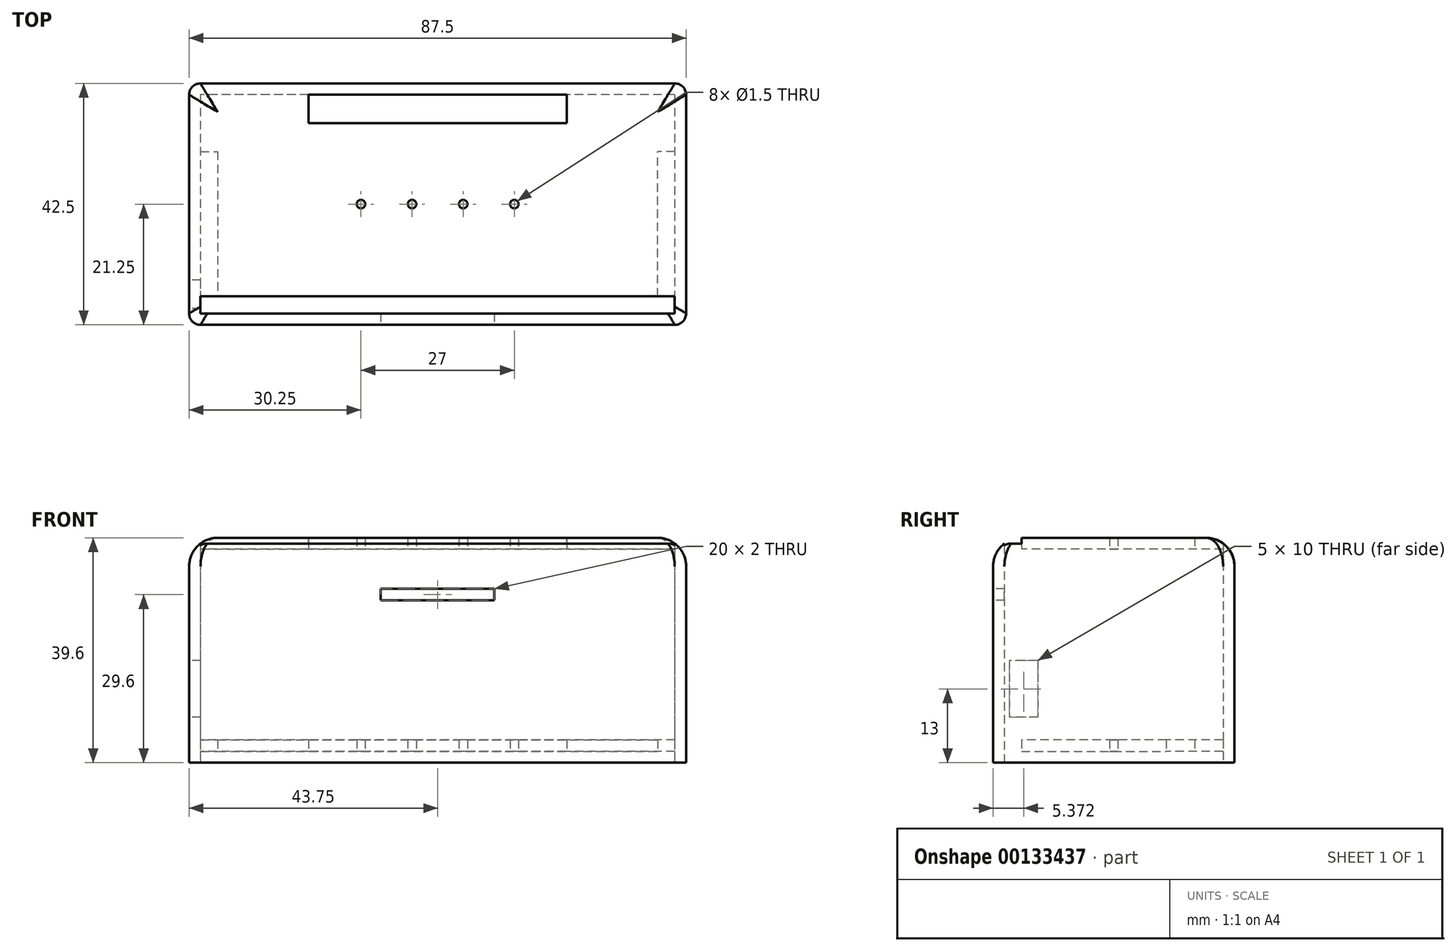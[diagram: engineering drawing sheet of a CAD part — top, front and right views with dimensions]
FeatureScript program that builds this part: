
annotation { "Feature Type Name" : "Feature", "Feature Type Description" : "" }
export const myFeature = defineFeature(function(context is Context, id is Id, definition is map)
    precondition{}
    {
        {
            var Q0;
            Q0=qCreatedBy(makeId("Top.planeOp"),FACE);
            var sketch = newSketch(context, id + "F0", { "sketchPlane" : qUnion([Q0])});
            skLineSegment(sketch, "E0.bottom", {"start": v(43.75, 21.25) * mm, "end": v(-43.75, 21.25) * mm});
            skLineSegment(sketch, "E0.top", {"start": v(43.75, -21.25) * mm, "end": v(-43.75, -21.25) * mm});
            skLineSegment(sketch, "E0.left", {"start": v(43.75, 21.25) * mm, "end": v(43.75, -21.25) * mm});
            skLineSegment(sketch, "E0.right", {"start": v(-43.75, 21.25) * mm, "end": v(-43.75, -21.25) * mm});
            skPoint(sketch, "E0.middle", {"position": v(0, 0) * mm});
            skLineSegment(sketch, "E1.0", {"start": v(-41.75, 19.25) * mm, "end": v(-41.75, -19.25) * mm});
            skLineSegment(sketch, "E1.1", {"start": v(41.75, 19.25) * mm, "end": v(-41.75, 19.25) * mm});
            skLineSegment(sketch, "E1.2", {"start": v(41.75, 19.25) * mm, "end": v(41.75, -19.25) * mm});
            skLineSegment(sketch, "E1.3", {"start": v(41.75, -19.25) * mm, "end": v(-41.75, -19.25) * mm});
            skLineSegment(sketch, "E2", {"start": v(0, 0) * mm, "end": v(4.5, 0) * mm});
            skLineSegment(sketch, "E3", {"start": v(4.5, 0) * mm, "end": v(13.5, 0) * mm});
            skCircle(sketch, "E4", {"center": v(4.5, 0) * mm, "radius": 0.75 * mm});
            skCircle(sketch, "E5", {"center": v(13.5, 0) * mm, "radius": 0.75 * mm});
            skCircle(sketch, "E6.MirrorC", {"center": v(-4.5, 0) * mm, "radius": 0.75 * mm});
            skCircle(sketch, "E7.MirrorC", {"center": v(-13.5, 0) * mm, "radius": 0.75 * mm});
            skLineSegment(sketch, "E8.bottom", {"start": v(-41.75, -19.25) * mm, "end": v(41.75, -19.25) * mm});
            skLineSegment(sketch, "E8.top", {"start": v(-41.75, -16.25) * mm, "end": v(41.75, -16.25) * mm});
            skLineSegment(sketch, "E8.left", {"start": v(-41.75, -19.25) * mm, "end": v(-41.75, -16.25) * mm});
            skLineSegment(sketch, "E8.right", {"start": v(41.75, -19.25) * mm, "end": v(41.75, -16.25) * mm});
            skLineSegment(sketch, "E9", {"start": v(-41.75, -16.25) * mm, "end": v(-38.75, -16.25) * mm});
            skLineSegment(sketch, "E10", {"start": v(-38.75, -16.25) * mm, "end": v(-38.75, 0) * mm});
            skLineSegment(sketch, "E11", {"start": v(41.75, -16.25) * mm, "end": v(38.75, -16.25) * mm});
            skLineSegment(sketch, "E12", {"start": v(38.75, -16.25) * mm, "end": v(38.75, -16.25) * mm});
            skLineSegment(sketch, "E13", {"start": v(38.75, -16.25) * mm, "end": v(38.75, 0) * mm});
            skLineSegment(sketch, "E14", {"start": v(-41.75, -16.25) * mm, "end": v(-41.75, 0) * mm});
            skLineSegment(sketch, "E15", {"start": v(-41.75, 19.25) * mm, "end": v(-22.75, 19.25) * mm});
            skLineSegment(sketch, "E16", {"start": v(-22.75, 19.25) * mm, "end": v(-22.75, 14.25) * mm});
            skLineSegment(sketch, "E17", {"start": v(41.75, 19.25) * mm, "end": v(22.75, 19.25) * mm});
            skLineSegment(sketch, "E18", {"start": v(22.75, 19.25) * mm, "end": v(22.75, 14.25) * mm});
            skLineSegment(sketch, "E19", {"start": v(22.75, 14.25) * mm, "end": v(-22.75, 14.25) * mm});
            skLineSegment(sketch, "E20", {"start": v(-41.75, 19.25) * mm, "end": v(-41.75, 9.25) * mm});
            skLineSegment(sketch, "E21", {"start": v(-41.75, 9.25) * mm, "end": v(-38.75, 9.25) * mm});
            skLineSegment(sketch, "E22", {"start": v(-38.75, 9.25) * mm, "end": v(-38.75, 0) * mm});
            skLineSegment(sketch, "E23", {"start": v(41.75, 19.25) * mm, "end": v(41.75, 9.25) * mm});
            skLineSegment(sketch, "E24", {"start": v(41.75, 9.25) * mm, "end": v(38.75, 9.25) * mm});
            skLineSegment(sketch, "E25", {"start": v(38.75, 9.25) * mm, "end": v(38.75, 0) * mm});
            skLineSegment(sketch, "E26", {"start": v(-41.75, 0) * mm, "end": v(-41.75, -19.25) * mm});
            skSolve(sketch);
        }
        {
            var Q0;
            Q0=makeQuery(id+"F0.imprint","IMPRINT",FACE,{"disambiguationData":[TD([[makeQuery(id+"F0.imprint","IMPRINT",EDGE,{"derivedFrom":sQuery(id+"F0.wireOp",EDGE,"E0.bottom")}),1.0]])]});
            extrude(context, id + "F1", {"entities" : qUnion([Q0]), "depth" : 39.6 * mm});
        }
        {
            var Q0;
            Q0=makeQuery(id+"F0.imprint","IMPRINT",FACE,{"disambiguationData":[TD([[makeQuery(id+"F0.imprint","IMPRINT",EDGE,{"derivedFrom":sQuery(id+"F0.wireOp",EDGE,"E1.0")}),1.0]])]});
            var Q1;
            Q1=makeQuery(id+"F0.imprint","IMPRINT",FACE,{"disambiguationData":[TD([[makeQuery(id+"F0.imprint","IMPRINT",EDGE,{"derivedFrom":sQuery(id+"F0.wireOp",EDGE,"E5")}),-1.0]])]});
            var Q2;
            Q2=makeQuery(id+"F0.imprint","IMPRINT",FACE,{"disambiguationData":[TD([[makeQuery(id+"F0.imprint","IMPRINT",EDGE,{"derivedFrom":sQuery(id+"F0.wireOp",EDGE,"E1.2")}),-1.0]])]});
            var Q3;
            Q3=makeQuery(id+"F0.imprint","IMPRINT",FACE,{"disambiguationData":[TD([[makeQuery(id+"F0.imprint","IMPRINT",EDGE,{"derivedFrom":sQuery(id+"F0.wireOp",EDGE,"E1.1")}),1.0]])]});
            var Q4;
            Q4=makeQuery(id+"F0.imprint","IMPRINT",FACE,{"disambiguationData":[TD([[makeQuery(id+"F0.imprint","IMPRINT",EDGE,{"derivedFrom":sQuery(id+"F0.wireOp",EDGE,"E8.bottom")}),1.0]])]});
            extrude(context, id + "F2", {"entities" : qUnion([Q0, Q1, Q2, Q3, Q4]), "operationType" : NewBodyOperationType.ADD, "depth" : 39.6 * mm, "hasSecondDirection" : true, "secondDirectionOppositeDirection" : false, "secondDirectionDepth" : 37.6 * mm});
        }
        {
            var Q0;
            Q0 = qSketchRegion(id + "F0", true);
            var Q1;
            Q1=makeQuery(id+"F0.imprint","IMPRINT",FACE,{"disambiguationData":[TD([[makeQuery(id+"F0.imprint","IMPRINT",EDGE,{"derivedFrom":sQuery(id+"F0.wireOp",EDGE,"E9")}),1.0]])]});
            var Q2;
            Q2=makeQuery(id+"F0.imprint","IMPRINT",FACE,{"disambiguationData":[TD([[makeQuery(id+"F0.imprint","IMPRINT",EDGE,{"derivedFrom":sQuery(id+"F0.wireOp",EDGE,"E8.bottom")}),1.0]])]});
            var Q3;
            {var subQ0=sQuery(id+"F0.wireOp",EDGE,"E11");Q3=makeQuery(id+"F0.imprint","IMPRINT",FACE,{"disambiguationData":[TD([[makeQuery(id+"F0.imprint","IMPRINT",EDGE,{"derivedFrom":subQ0}),-1.0]])]});}
            var Q4;
            Q4=makeQuery(id+"F0.imprint","IMPRINT",FACE,{"disambiguationData":[TD([[makeQuery(id+"F0.imprint","IMPRINT",EDGE,{"derivedFrom":sQuery(id+"F0.wireOp",EDGE,"E1.1")}),1.0]])]});
            extrude(context, id + "F3", {"entities" : qUnion([Q0, Q1, Q2, Q3, Q4]), "operationType" : NewBodyOperationType.ADD, "depth" : 4 * mm, "hasSecondDirection" : true, "secondDirectionOppositeDirection" : false, "secondDirectionDepth" : 2 * mm});
        }
        {
            var Q0;
            Q0=makeQuery(id+"F1.opExtrude","SWEPT_EDGE",EDGE,{"disambiguationData":[OSD([sQuery(id+"F0.wireOp",EDGE,"E0.bottom"),sQuery(id+"F0.wireOp",EDGE,"E0.left")])]});
            var Q1;
            Q1=makeQuery(id+"F1.opExtrude","SWEPT_EDGE",EDGE,{"disambiguationData":[OSD([sQuery(id+"F0.wireOp",EDGE,"E0.bottom"),sQuery(id+"F0.wireOp",EDGE,"E0.right")])]});
            var Q2;
            Q2=makeQuery(id+"F1.opExtrude","SWEPT_EDGE",EDGE,{"disambiguationData":[OSD([sQuery(id+"F0.wireOp",EDGE,"E0.top"),sQuery(id+"F0.wireOp",EDGE,"E0.left")])]});
            var Q3;
            Q3=makeQuery(id+"F1.opExtrude","SWEPT_EDGE",EDGE,{"disambiguationData":[OSD([sQuery(id+"F0.wireOp",EDGE,"E0.top"),sQuery(id+"F0.wireOp",EDGE,"E0.right")])]});
            fillet(context, id + "F4", {"entities" : qUnion([Q0, Q1, Q2, Q3]), "radius" : 2 * mm, "tangentPropagation" : true, "allowEdgeOverflow" : false});
        }
        {
            var Q0;
            Q0=makeQuery(id+"F1.opExtrude","CAP_EDGE",EDGE,{"disambiguationData":[OSD([sQuery(id+"F0.wireOp",EDGE,"E0.left")])],"isStart":false});
            fillet(context, id + "F5", {"entities" : qUnion([Q0]), "radius" : 5 * mm, "tangentPropagation" : true, "allowEdgeOverflow" : false});
        }
        {
            var Q0;
            Q0=makeQuery(id+"F1.opExtrude","SWEPT_FACE",FACE,{"disambiguationData":[OSD([sQuery(id+"F0.wireOp",EDGE,"E0.top")])]});
            var sketch = newSketch(context, id + "F6", { "sketchPlane" : qUnion([Q0])});
            skLineSegment(sketch, "E27", {"start": v(0, 0) * mm, "end": v(0, 34.6) * mm});
            skLineSegment(sketch, "E28", {"start": v(0, 34.6) * mm, "end": v(0, 29.6) * mm});
            skLineSegment(sketch, "E29.bottom", {"start": v(10, 28.6) * mm, "end": v(-10, 28.6) * mm});
            skLineSegment(sketch, "E29.top", {"start": v(10, 30.6) * mm, "end": v(-10, 30.6) * mm});
            skLineSegment(sketch, "E29.left", {"start": v(10, 28.6) * mm, "end": v(10, 30.6) * mm});
            skLineSegment(sketch, "E29.right", {"start": v(-10, 28.6) * mm, "end": v(-10, 30.6) * mm});
            skPoint(sketch, "E29.middle", {"position": v(0, 29.6) * mm});
            skSolve(sketch);
        }
        {
            var Q0;
            {var subQ0=sQuery(id+"F6.wireOp",EDGE,"E29.right");Q0=makeQuery(id+"F6.imprint","IMPRINT",FACE,{"disambiguationData":[TD([[makeQuery(id+"F6.imprint","IMPRINT",EDGE,{"derivedFrom":subQ0}),-1.0]])]});}
            var Q1;
            {var subQ0=sQuery(id+"F6.wireOp",EDGE,"E29.left");Q1=makeQuery(id+"F6.imprint","IMPRINT",FACE,{"disambiguationData":[TD([[makeQuery(id+"F6.imprint","IMPRINT",EDGE,{"derivedFrom":subQ0}),1.0]])]});}
            extrude(context, id + "F7", {"entities" : qUnion([Q0, Q1]), "operationType" : NewBodyOperationType.REMOVE, "oppositeDirection" : true, "depth" : 2 * mm});
        }
        {
            var Q0;
            Q0=makeQuery(id+"F1.opExtrude","SWEPT_FACE",FACE,{"disambiguationData":[OSD([sQuery(id+"F0.wireOp",EDGE,"E0.right")])]});
            var sketch = newSketch(context, id + "F8", { "sketchPlane" : qUnion([Q0])});
            skLineSegment(sketch, "E30", {"start": v(19.25, 0) * mm, "end": v(21.88, 0) * mm});
            skLineSegment(sketch, "E31", {"start": v(21.88, 0) * mm, "end": v(21.88, 13) * mm});
            skLineSegment(sketch, "E32", {"start": v(21.88, 13) * mm, "end": v(15.88, 13) * mm});
            skLineSegment(sketch, "E33.bottom", {"start": v(18.38, 8) * mm, "end": v(13.38, 8) * mm});
            skLineSegment(sketch, "E33.top", {"start": v(18.38, 18) * mm, "end": v(13.38, 18) * mm});
            skLineSegment(sketch, "E33.left", {"start": v(18.38, 8) * mm, "end": v(18.38, 18) * mm});
            skLineSegment(sketch, "E33.right", {"start": v(13.38, 8) * mm, "end": v(13.38, 18) * mm});
            skPoint(sketch, "E33.middle", {"position": v(15.88, 13) * mm});
            skSolve(sketch);
        }
        {
            var Q0;
            Q0 = qSketchRegion(id + "F8", true);
            extrude(context, id + "F9", {"entities" : qUnion([Q0]), "operationType" : NewBodyOperationType.REMOVE, "oppositeDirection" : true, "depth" : 5 * mm});
        }
    });
